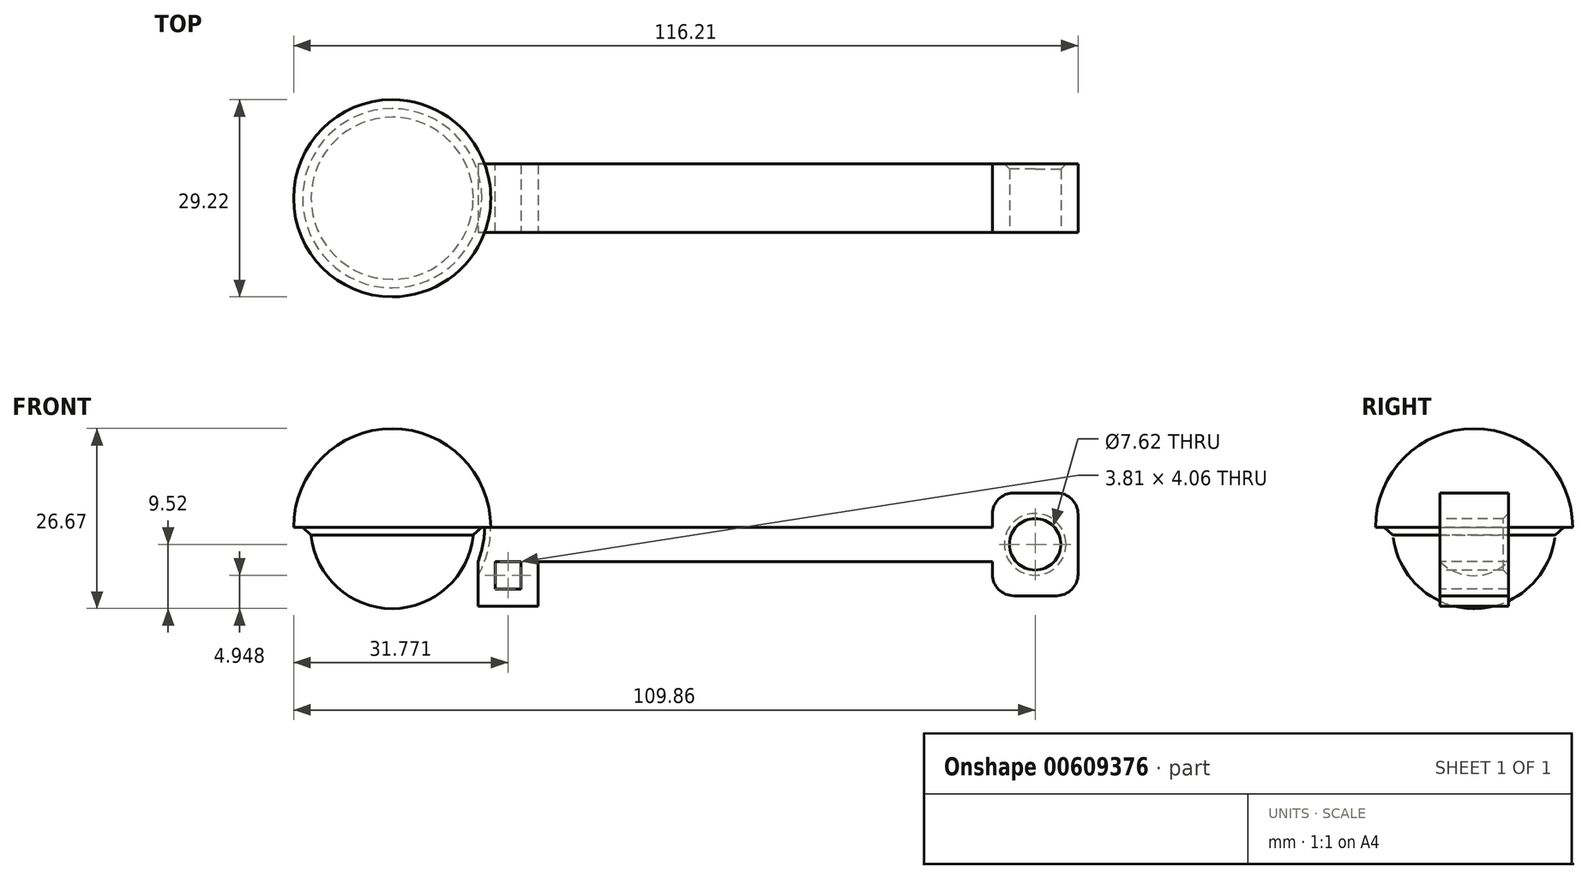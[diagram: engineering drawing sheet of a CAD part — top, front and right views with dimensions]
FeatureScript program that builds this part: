
annotation { "Feature Type Name" : "Feature", "Feature Type Description" : "" }
export const myFeature = defineFeature(function(context is Context, id is Id, definition is map)
    precondition{}
    {
        {
            var Q0;
            Q0=qCreatedBy(makeId("Top.planeOp"),FACE);
            var sketch = newSketch(context, id + "F0", { "sketchPlane" : qUnion([Q0])});
            skLineSegment(sketch, "E0.bottom", {"start": v(-50.8, -5.08) * mm, "end": v(50.8, -5.08) * mm});
            skLineSegment(sketch, "E0.top", {"start": v(-50.8, 5.08) * mm, "end": v(50.8, 5.08) * mm});
            skLineSegment(sketch, "E0.left", {"start": v(-50.8, -5.08) * mm, "end": v(-50.8, 5.08) * mm});
            skLineSegment(sketch, "E0.right", {"start": v(50.8, -5.08) * mm, "end": v(50.8, 5.08) * mm});
            skPoint(sketch, "E0.middle", {"position": v(0, 0) * mm});
            skSolve(sketch);
        }
        {
            var Q0;
            Q0 = qSketchRegion(id + "F0", true);
            var Q1;
            Q1 = qSketchRegion(id + "F2", true);
            extrude(context, id + "F1", {"entities" : qUnion([Q0, Q1]), "depth" : 5.08 * mm, "offsetDistance" : 25.4 * mm});
        }
        {
            var Q0;
            Q0=makeQuery(id+"F1.opExtrude","SWEPT_FACE",FACE,{"disambiguationData":[OSD([sQuery(id+"F0.wireOp",EDGE,"E0.bottom")])]});
            var sketch = newSketch(context, id + "F2", { "sketchPlane" : qUnion([Q0])});
            skLineSegment(sketch, "E1.bottom", {"start": v(50.8, -5.08) * mm, "end": v(38.1, -5.08) * mm});
            skLineSegment(sketch, "E1.top", {"start": v(50.8, 10.16) * mm, "end": v(38.1, 10.16) * mm});
            skLineSegment(sketch, "E1.left", {"start": v(50.8, -5.08) * mm, "end": v(50.8, 10.16) * mm});
            skLineSegment(sketch, "E1.right", {"start": v(38.1, -5.08) * mm, "end": v(38.1, 10.16) * mm});
            skPoint(sketch, "E1.middle", {"position": v(44.45, 2.54) * mm});
            skSolve(sketch);
        }
        {
            var Q0;
            Q0 = qSketchRegion(id + "F2", true);
            extrude(context, id + "F3", {"entities" : qUnion([Q0]), "operationType" : NewBodyOperationType.ADD, "oppositeDirection" : true, "depth" : 10.16 * mm, "offsetDistance" : 25.4 * mm});
        }
        {
            var Q0;
            Q0=makeQuery(id+"F1.opExtrude","CAP_FACE",FACE,{"disambiguationData":[OSD([sQuery(id+"F0.wireOp",EDGE,"E0.bottom"),sQuery(id+"F0.wireOp",EDGE,"E0.top"),sQuery(id+"F0.wireOp",EDGE,"E0.left"),sQuery(id+"F0.wireOp",EDGE,"E0.right")])],"isStart":false});
            var sketch = newSketch(context, id + "F4", { "sketchPlane" : qUnion([Q0])});
            skArc(sketch, "E2", {"start": v(-50.8, -14.6) * mm, "mid": v(-36.2, 0) * mm, "end": v(-50.8, 14.6) * mm});
            skLineSegment(sketch, "E3", {"start": v(-50.8, -14.6) * mm, "end": v(-50.8, 14.6) * mm, "construction": true});
            skLineSegment(sketch, "E4", {"start": v(-50.8, 14.6) * mm, "end": v(-50.8, -14.6) * mm});
            skLineSegment(sketch, "E5", {"start": v(-50.8, 0) * mm, "end": v(-50.8, 32.09) * mm, "construction": true});
            skSolve(sketch);
        }
        {
            var Q0;
            Q0 = qSketchRegion(id + "F4", true);
            var Q1;
            Q1=sQuery(id+"F4.wireOp",EDGE,"E5");
            revolve(context, id + "F5", {"operationType" : NewBodyOperationType.ADD, "entities" : qUnion([Q0]), "axis" : qUnion([Q1]), "revolveType" : RevolveType.ONE_DIRECTION, "angle" : 180 * degree});
        }
        {
            var Q0;
            Q0=makeQuery(id+"F5.boolean.opBoolean","MERGE",FACE,{"derivedFrom":[makeQuery(id+"F1.opExtrude","CAP_FACE",FACE,{"disambiguationData":[OSD([sQuery(id+"F0.wireOp",EDGE,"E0.bottom"),sQuery(id+"F0.wireOp",EDGE,"E0.top"),sQuery(id+"F0.wireOp",EDGE,"E0.left"),sQuery(id+"F0.wireOp",EDGE,"E0.right")])],"isStart":false}),makeQuery(id+"F5.opRevolve","CAP_FACE",FACE,{"disambiguationData":[OSD([sQuery(id+"F4.wireOp",EDGE,"E2"),sQuery(id+"F4.wireOp",EDGE,"E4")])],"isStart":true})]});
            var sketch = newSketch(context, id + "F6", { "sketchPlane" : qUnion([Q0])});
            skArc(sketch, "E6", {"start": v(-50.8, -12.06) * mm, "mid": v(-38.73, 0) * mm, "end": v(-50.8, 12.07) * mm});
            skLineSegment(sketch, "E7", {"start": v(-50.8, 0) * mm, "end": v(-50.8, -25.53) * mm, "construction": true});
            skLineSegment(sketch, "E8", {"start": v(-50.8, -25.53) * mm, "end": v(-50.8, 19.01) * mm, "construction": true});
            skLineSegment(sketch, "E9", {"start": v(-50.8, 12.07) * mm, "end": v(-50.8, -12.06) * mm});
            skSolve(sketch);
        }
        {
            var Q0;
            Q0 = qSketchRegion(id + "F6", true);
            var Q1;
            Q1=sQuery(id+"F6.wireOp",EDGE,"E8");
            revolve(context, id + "F7", {"operationType" : NewBodyOperationType.REMOVE, "entities" : qUnion([Q0]), "axis" : qUnion([Q1]), "revolveType" : RevolveType.FULL, "oppositeDirection" : true});
        }
        {
            var Q0;
            Q0=makeQuery(id+"F3.boolean.opBoolean","MERGE",FACE,{"derivedFrom":[makeQuery(id+"F1.opExtrude","SWEPT_FACE",FACE,{"disambiguationData":[OSD([sQuery(id+"F0.wireOp",EDGE,"E0.bottom")])]}),makeQuery(id+"F3.opExtrude","CAP_FACE",FACE,{"disambiguationData":[OSD([sQuery(id+"F2.wireOp",EDGE,"E1.bottom"),sQuery(id+"F2.wireOp",EDGE,"E1.top"),sQuery(id+"F2.wireOp",EDGE,"E1.left"),sQuery(id+"F2.wireOp",EDGE,"E1.right")])],"isStart":true})]});
            var sketch = newSketch(context, id + "F8", { "sketchPlane" : qUnion([Q0])});
            skLineSegment(sketch, "E10.bottom", {"start": v(-35.54, -4.06) * mm, "end": v(-38.08, -4.06) * mm});
            skLineSegment(sketch, "E10.top", {"start": v(-35.54, 4.06) * mm, "end": v(-38.08, 4.06) * mm});
            skLineSegment(sketch, "E10.left", {"start": v(-35.54, -4.06) * mm, "end": v(-35.54, 4.06) * mm});
            skLineSegment(sketch, "E10.right", {"start": v(-38.08, -4.06) * mm, "end": v(-38.08, 4.06) * mm});
            skPoint(sketch, "E10.middle", {"position": v(-36.81, 0) * mm});
            skLineSegment(sketch, "E11.bottom", {"start": v(-31.73, 4.06) * mm, "end": v(-29.2, 4.06) * mm});
            skLineSegment(sketch, "E11.top", {"start": v(-31.73, -4.06) * mm, "end": v(-29.2, -4.06) * mm});
            skLineSegment(sketch, "E11.left", {"start": v(-31.73, 4.06) * mm, "end": v(-31.73, -4.06) * mm});
            skLineSegment(sketch, "E11.right", {"start": v(-29.2, 4.06) * mm, "end": v(-29.2, -4.06) * mm});
            skPoint(sketch, "E11.middle", {"position": v(-30.46, 0) * mm});
            skLineSegment(sketch, "E12.bottom", {"start": v(-38.08, -4.06) * mm, "end": v(-29.2, -4.06) * mm});
            skLineSegment(sketch, "E12.top", {"start": v(-38.08, -6.6) * mm, "end": v(-29.2, -6.6) * mm});
            skLineSegment(sketch, "E12.left", {"start": v(-38.08, -4.06) * mm, "end": v(-38.08, -6.6) * mm});
            skLineSegment(sketch, "E12.right", {"start": v(-29.2, -4.06) * mm, "end": v(-29.2, -6.6) * mm});
            skSolve(sketch);
        }
        {
            var Q0;
            Q0 = qSketchRegion(id + "F8", true);
            extrude(context, id + "F9", {"entities" : qUnion([Q0]), "operationType" : NewBodyOperationType.ADD, "oppositeDirection" : true, "depth" : 10.16 * mm, "offsetDistance" : 25.4 * mm});
        }
        {
            var Q0;
            Q0=makeQuery(id+"F7.boolean.opBoolean","INTERSECT",EDGE,{"derivedFrom":[makeQuery(id+"F5.boolean.opBoolean","MERGE",FACE,{"derivedFrom":[makeQuery(id+"F1.opExtrude","CAP_FACE",FACE,{"disambiguationData":[OSD([sQuery(id+"F0.wireOp",EDGE,"E0.bottom"),sQuery(id+"F0.wireOp",EDGE,"E0.top"),sQuery(id+"F0.wireOp",EDGE,"E0.left"),sQuery(id+"F0.wireOp",EDGE,"E0.right")])],"isStart":false}),makeQuery(id+"F5.opRevolve","CAP_FACE",FACE,{"disambiguationData":[OSD([sQuery(id+"F4.wireOp",EDGE,"E2"),sQuery(id+"F4.wireOp",EDGE,"E4")])],"isStart":true})]}),makeQuery(id+"F7.opRevolve","SWEPT_FACE",FACE,{"disambiguationData":[OSD([sQuery(id+"F6.wireOp",EDGE,"E6")])]})]});
            chamfer(context, id + "F10", {"entities" : qUnion([Q0]), "width" : 1.27 * mm, "tangentPropagation" : true});
        }
        {
            var Q0;
            Q0=makeQuery(id+"F3.boolean.opBoolean","MERGE",FACE,{"derivedFrom":[makeQuery(id+"F1.opExtrude","SWEPT_FACE",FACE,{"disambiguationData":[OSD([sQuery(id+"F0.wireOp",EDGE,"E0.bottom")])]}),makeQuery(id+"F3.opExtrude","CAP_FACE",FACE,{"disambiguationData":[OSD([sQuery(id+"F2.wireOp",EDGE,"E1.bottom"),sQuery(id+"F2.wireOp",EDGE,"E1.top"),sQuery(id+"F2.wireOp",EDGE,"E1.left"),sQuery(id+"F2.wireOp",EDGE,"E1.right")])],"isStart":true})]});
            var sketch = newSketch(context, id + "F11", { "sketchPlane" : qUnion([Q0])});
            skCircle(sketch, "E13", {"center": v(44.45, 2.54) * mm, "radius": 3.81 * mm});
            skSolve(sketch);
        }
        {
            var Q0;
            Q0 = qSketchRegion(id + "F11", true);
            extrude(context, id + "F12", {"entities" : qUnion([Q0]), "operationType" : NewBodyOperationType.REMOVE, "oppositeDirection" : true, "depth" : 25.4 * mm, "offsetDistance" : 25.4 * mm});
        }
        {
            var Q0;
            Q0=makeQuery(id+"F12.boolean.opBoolean","INTERSECT",EDGE,{"derivedFrom":[makeQuery(id+"F9.boolean.opBoolean","MERGE",FACE,{"derivedFrom":[makeQuery(id+"F3.boolean.opBoolean","MERGE",FACE,{"derivedFrom":[makeQuery(id+"F1.opExtrude","SWEPT_FACE",FACE,{"disambiguationData":[OSD([sQuery(id+"F0.wireOp",EDGE,"E0.top")])]}),makeQuery(id+"F3.opExtrude","CAP_FACE",FACE,{"disambiguationData":[OSD([sQuery(id+"F2.wireOp",EDGE,"E1.bottom"),sQuery(id+"F2.wireOp",EDGE,"E1.top"),sQuery(id+"F2.wireOp",EDGE,"E1.left"),sQuery(id+"F2.wireOp",EDGE,"E1.right")])],"isStart":false})]}),makeQuery(id+"F9.opExtrude","CAP_FACE",FACE,{"disambiguationData":[OSD([sQuery(id+"F8.wireOp",EDGE,"E10.bottom"),sQuery(id+"F8.wireOp",EDGE,"E10.top"),sQuery(id+"F8.wireOp",EDGE,"E10.left"),sQuery(id+"F8.wireOp",EDGE,"E10.right")])],"isStart":false}),makeQuery(id+"F9.opExtrude","CAP_FACE",FACE,{"disambiguationData":[OSD([sQuery(id+"F8.wireOp",EDGE,"E11.bottom"),sQuery(id+"F8.wireOp",EDGE,"E11.top"),sQuery(id+"F8.wireOp",EDGE,"E11.left"),sQuery(id+"F8.wireOp",EDGE,"E11.right")])],"isStart":false})]}),makeQuery(id+"F12.opExtrude","SWEPT_FACE",FACE,{"disambiguationData":[OSD([sQuery(id+"F11.wireOp",EDGE,"E13")])]})]});
            var Q1;
            Q1=makeQuery(id+"F12.boolean.opBoolean","COPY",EDGE,{"derivedFrom":makeQuery(id+"F12.opExtrude","CAP_EDGE",EDGE,{"disambiguationData":[OSD([sQuery(id+"F11.wireOp",EDGE,"E13")])],"isStart":true})});
            chamfer(context, id + "F13", {"entities" : qUnion([Q0, Q1]), "width" : 0.76 * mm, "tangentPropagation" : true});
        }
        {
            var Q0;
            Q0=makeQuery(id+"F3.opExtrude","SWEPT_EDGE",EDGE,{"disambiguationData":[OSD([sQuery(id+"F2.wireOp",EDGE,"E1.bottom"),sQuery(id+"F2.wireOp",EDGE,"E1.left")])]});
            var Q1;
            Q1=makeQuery(id+"F3.opExtrude","SWEPT_EDGE",EDGE,{"disambiguationData":[OSD([sQuery(id+"F2.wireOp",EDGE,"E1.bottom"),sQuery(id+"F2.wireOp",EDGE,"E1.right")])]});
            var Q2;
            Q2=makeQuery(id+"F3.opExtrude","SWEPT_EDGE",EDGE,{"disambiguationData":[OSD([sQuery(id+"F2.wireOp",EDGE,"E1.top"),sQuery(id+"F2.wireOp",EDGE,"E1.right")])]});
            var Q3;
            Q3=makeQuery(id+"F3.opExtrude","SWEPT_EDGE",EDGE,{"disambiguationData":[OSD([sQuery(id+"F2.wireOp",EDGE,"E1.top"),sQuery(id+"F2.wireOp",EDGE,"E1.left")])]});
            fillet(context, id + "F14", {"entities" : qUnion([Q0, Q1, Q2, Q3]), "radius" : 3.17 * mm, "tangentPropagation" : true, "allowEdgeOverflow" : false});
        }
    });
